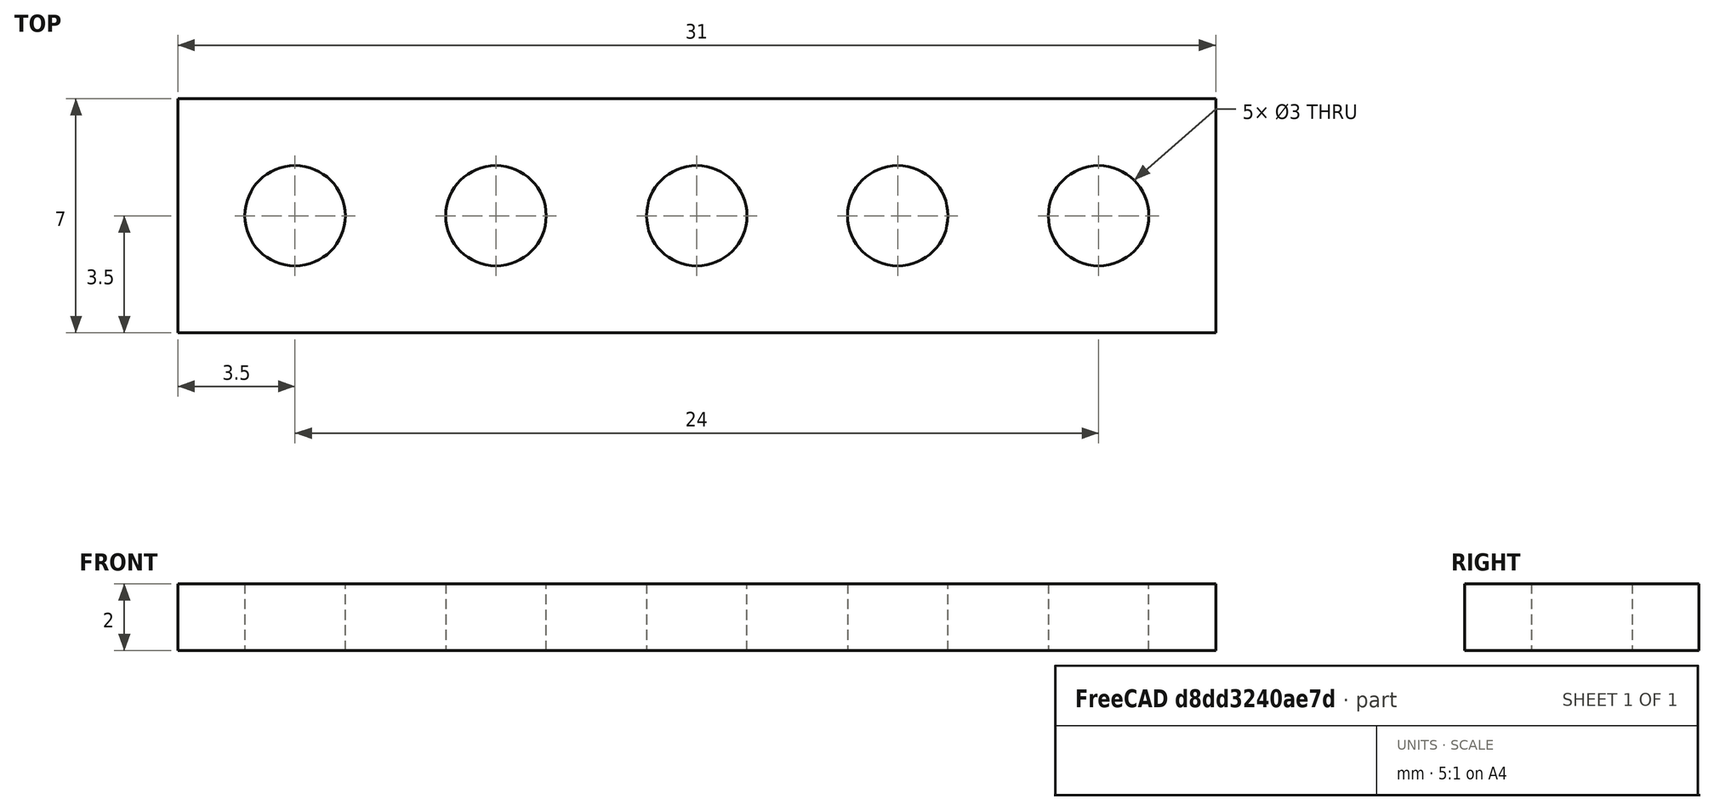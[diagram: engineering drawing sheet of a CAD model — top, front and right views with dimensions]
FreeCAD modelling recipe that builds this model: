
FCSTD DOCUMENT  (FreeCAD 0.21R33694 (Git))
Label: OJT1_T10P01_mecano
License: All rights reserved
LicenseURL: https://en.wikipedia.org/wiki/All_rights_reserved
objects: Part::Cylinder×5, Part::Box×1, Part::MultiFuse×1, Part::Cut×1
note: 8 computed .brp shape members not serialized (recipe doc carries the construction recipe); baked Part::Feature solids carry a one-line shape summary decoded from their .brp

FEATURE [Part::Box] Box  label="Base"
  AttacherType = Attacher::AttachEngine3D
  Height = 2
  Length = 31
  Width = 7
FEATURE [Part::Cylinder] Cylinder  label="Forat_1"
  Angle = 360
  AttacherType = Attacher::AttachEngine3D
  FirstAngle = 0
  Height = 2
  Placement = pos=(3.5,3.5,0) rot=(0,0,1;0rad)
  Radius = 1.5
  SecondAngle = 0
FEATURE [Part::Cylinder] Cylinder001  label="Forat_002"
  Angle = 360
  AttacherType = Attacher::AttachEngine3D
  FirstAngle = 0
  Height = 2
  Placement = pos=(9.5,3.5,0) rot=(0,0,1;0rad)
  Radius = 1.5
  SecondAngle = 0
FEATURE [Part::Cylinder] Cylinder002  label="Forat_003"
  Angle = 360
  AttacherType = Attacher::AttachEngine3D
  FirstAngle = 0
  Height = 2
  Placement = pos=(15.5,3.5,0) rot=(0,0,1;0rad)
  Radius = 1.5
  SecondAngle = 0
FEATURE [Part::Cylinder] Cylinder003  label="Forat_004"
  Angle = 360
  AttacherType = Attacher::AttachEngine3D
  FirstAngle = 0
  Height = 2
  Placement = pos=(21.5,3.5,0) rot=(0,0,1;0rad)
  Radius = 1.5
  SecondAngle = 0
FEATURE [Part::Cylinder] Cylinder004  label="Forat_005"
  Angle = 360
  AttacherType = Attacher::AttachEngine3D
  FirstAngle = 0
  Height = 2
  Placement = pos=(27.5,3.5,0) rot=(0,0,1;0rad)
  Radius = 1.5
  SecondAngle = 0
FEATURE [Part::MultiFuse] Fusion
  Shapes = -> [Cylinder,Cylinder001,Cylinder002,Cylinder003,Cylinder004]
FEATURE [Part::Cut] Cut  label="Mecano"
  Base = -> Box
  Tool = -> Fusion
